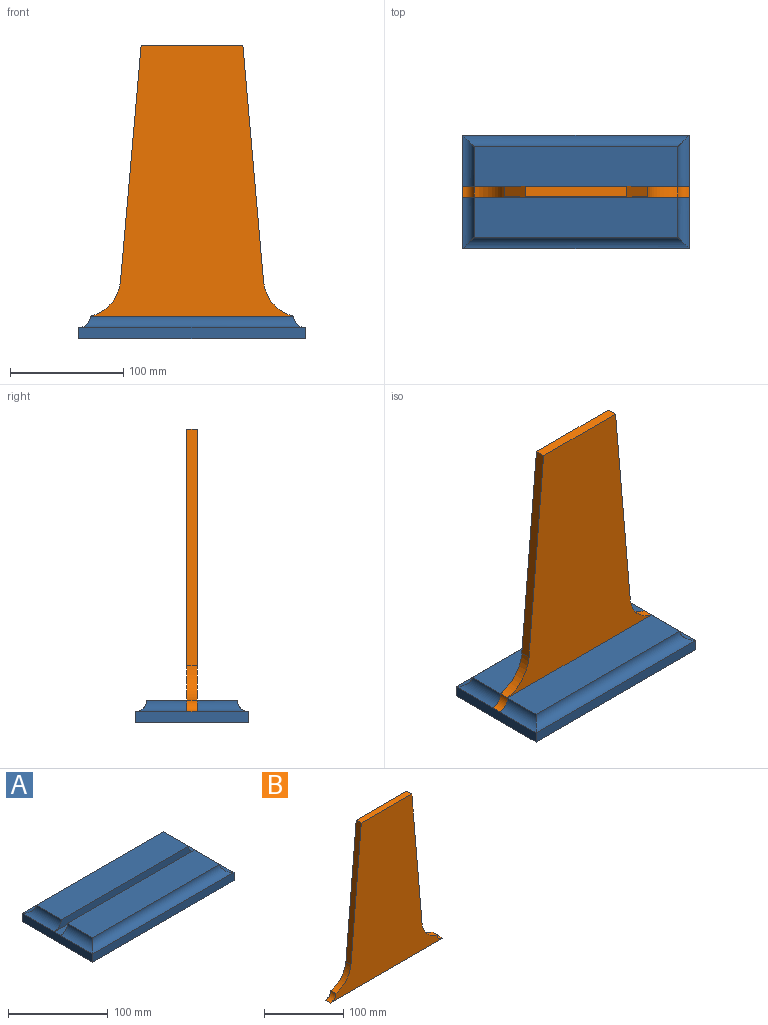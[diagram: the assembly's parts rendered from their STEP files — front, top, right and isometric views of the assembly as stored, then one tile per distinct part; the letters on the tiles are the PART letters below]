
ASSEMBLY  parts=2 mates=1
PART A: 16 faces, bbox 200x100x20 mm
  f0: plane 180x35.5mm, normal (0,0,1), area 6390mm2, adj f1,f8,f12,f14
  f1: cylinder r=10mm len=200mm, axis (-1,0,0), area 2941.6mm2, adj f0,f9,f12,f14
  f2: cylinder r=10mm len=200mm, axis (-1,0,0), area 2941.6mm2, adj f3,f11,f13,f15
  f3: plane 180x35.5mm, normal (0,0,1), area 6390mm2, adj f2,f6,f13,f15
  f4: plane 100x10mm, normal (1,0,0), area 1000mm2, adj f7,f9,f10,f11,f14,f15
  f5: plane 100x10mm, normal (-1,0,0), area 1000mm2, adj f7,f9,f10,f11,f12,f13
  f6: plane 200x10mm, normal (0,-1,0), area 1842.9mm2, adj f3,f7,f13,f15
  f7: plane 200x9mm, normal (0,0,1), area 1800mm2, adj f4,f5,f6,f8
  f8: plane 200x10mm, normal (0,1,0), area 1842.9mm2, adj f0,f7,f12,f14
  f9: plane 200x10mm, normal (0,-1,0), area 2000mm2, adj f1,f4,f5,f10
  f10: plane 200x100mm, normal (0,0,-1), area 20000mm2, adj f4,f5,f9,f11
  f11: plane 200x10mm, normal (0,1,0), area 2000mm2, adj f2,f4,f5,f10
  f12: cylinder r=10mm len=45.5mm, axis (0,1,0), area 614.7mm2, adj f0,f1,f5,f8
  f13: cylinder r=10mm len=45.5mm, axis (0,1,0), area 614.7mm2, adj f2,f3,f5,f6
  f14: cylinder r=10mm len=45.5mm, axis (0,1,0), area 614.7mm2, adj f0,f1,f4,f8
  f15: cylinder r=10mm len=45.5mm, axis (0,1,0), area 614.7mm2, adj f2,f3,f4,f6
PART B: 10 faces, bbox 200x9x250 mm
  f0: plane 90x9mm, normal (0,0,1), area 810mm2, adj f1,f5,f6,f7
  f1: plane 209.01x18.29mm, normal (-1,0,0.09), area 1888.3mm2, adj f0,f2,f5,f6
  f2: cylinder r=35mm len=30.99mm, axis (0,1,0), area 393.3mm2, adj f1,f3,f5,f6
  f3: cylinder r=10mm len=10mm, axis (0,1,0), area 141.4mm2, adj f2,f4,f5,f6
  f4: plane 200x9mm, normal (0,0,-1), area 1800mm2, adj f3,f5,f6,f9
  f5: plane 250x200mm, normal (0,-1,0), area 28858.6mm2, adj f0,f1,f2,f3,f4,f7,f8,f9
  f6: plane 250x200mm, normal (0,1,0), area 28858.6mm2, adj f0,f1,f2,f3,f4,f7,f8,f9
  f7: plane 209.01x18.29mm, normal (1,0,0.09), area 1888.3mm2, adj f0,f5,f6,f8
  f8: cylinder r=35mm len=30.99mm, axis (0,1,0), area 393.3mm2, adj f5,f6,f7,f9
  f9: cylinder r=10mm len=10mm, axis (0,1,0), area 141.4mm2, adj f4,f5,f6,f8
PLACE A t=(-4.26,0.11,3.85)mm
PLACE B t=(-4.26,0.11,13.85)mm
MATE fastened B.f4 <-> A.f7  axis (0,0,-1) through (-4.26,0.11,13.85)mm
